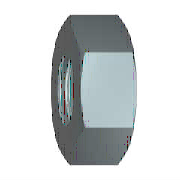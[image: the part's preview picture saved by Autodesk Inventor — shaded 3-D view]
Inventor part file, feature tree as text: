
AUTODESK INVENTOR PART (.ipt)
format: ipt  version: 2023 (Build 270158000, 158)  size: 170,496 bytes
history: native  units: mm (DEFAULTED — no unit token found)
features: sketch x3, other x2, extrude x1, hole x1, plane x1
ambient origin geometry x7: Origin, YZ Plane, XZ Plane, X Axis, Y Axis, Z Axis, Center Point
bodies: Solid1 (feature_tree)
feature tree (8):
  extrude  "Базовый элемент"  Depth=15.011107mm
  other  "Фаска1"
  hole  "Резьба"  [1 undecoded]
  other  "Work Axis1"
  plane  "Work Plane1"
  sketch  "Эскиз1"
  sketch  "Эскиз2"
  sketch  "Эскиз3"
note: 1 required parameter value undecoded (feature->parameter linkage not recoverable at this tier; creation-order binding heuristic only, values carry confidence <= 0.55)
